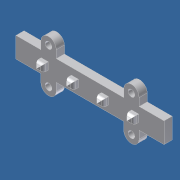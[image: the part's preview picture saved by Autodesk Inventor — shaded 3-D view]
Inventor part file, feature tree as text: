
AUTODESK INVENTOR PART (.ipt)
format: ipt  version: unknown  size: 417,280 bytes
history: native  units: in
note: dims shown in document units (in); Inventor stores cm internally (conversion verified against a paired STEP export)
features: extrude x5, sketch x5, chamfer x1, fillet x1
ambient origin geometry x8: Origin, YZ Plane, XZ Plane, XY Plane, X Axis, Y Axis, Z Axis, Center Point
feature tree (12):
  extrude  "Extrusion2"  Depth=0.2in TaperAngle=0.0deg
  extrude  "Extrusion3"  Depth=0.085in TaperAngle=45.0deg
  extrude  "Extrusion4"  Depth=0.2in TaperAngle=0.0deg
  chamfer  "Chamfer1"  Distance=1.0in
  fillet  "Fillet1"  [1 undecoded]
  extrude  "Extrusion7"  [1 undecoded]
  extrude  "Extrusion8"  [1 undecoded]
  sketch  "Sketch1"  dims[d14=0.2in d15=0.0in d16=0.2in d17=0.0in]
  sketch  "Sketch2"  dims[d18=0.2in d19=0.0in d20=0.085in d21=0.125in d22=45.0deg]
  sketch  "Sketch3"  dims[d23=0.125in d36=0.2in d37=0.0in d38=1.0in d39=0.0in]
  sketch  "Sketch4"
  sketch  "Sketch5"
note: 3 required parameter values undecoded (feature->parameter linkage not recoverable at this tier; creation-order binding heuristic only, values carry confidence <= 0.55)
